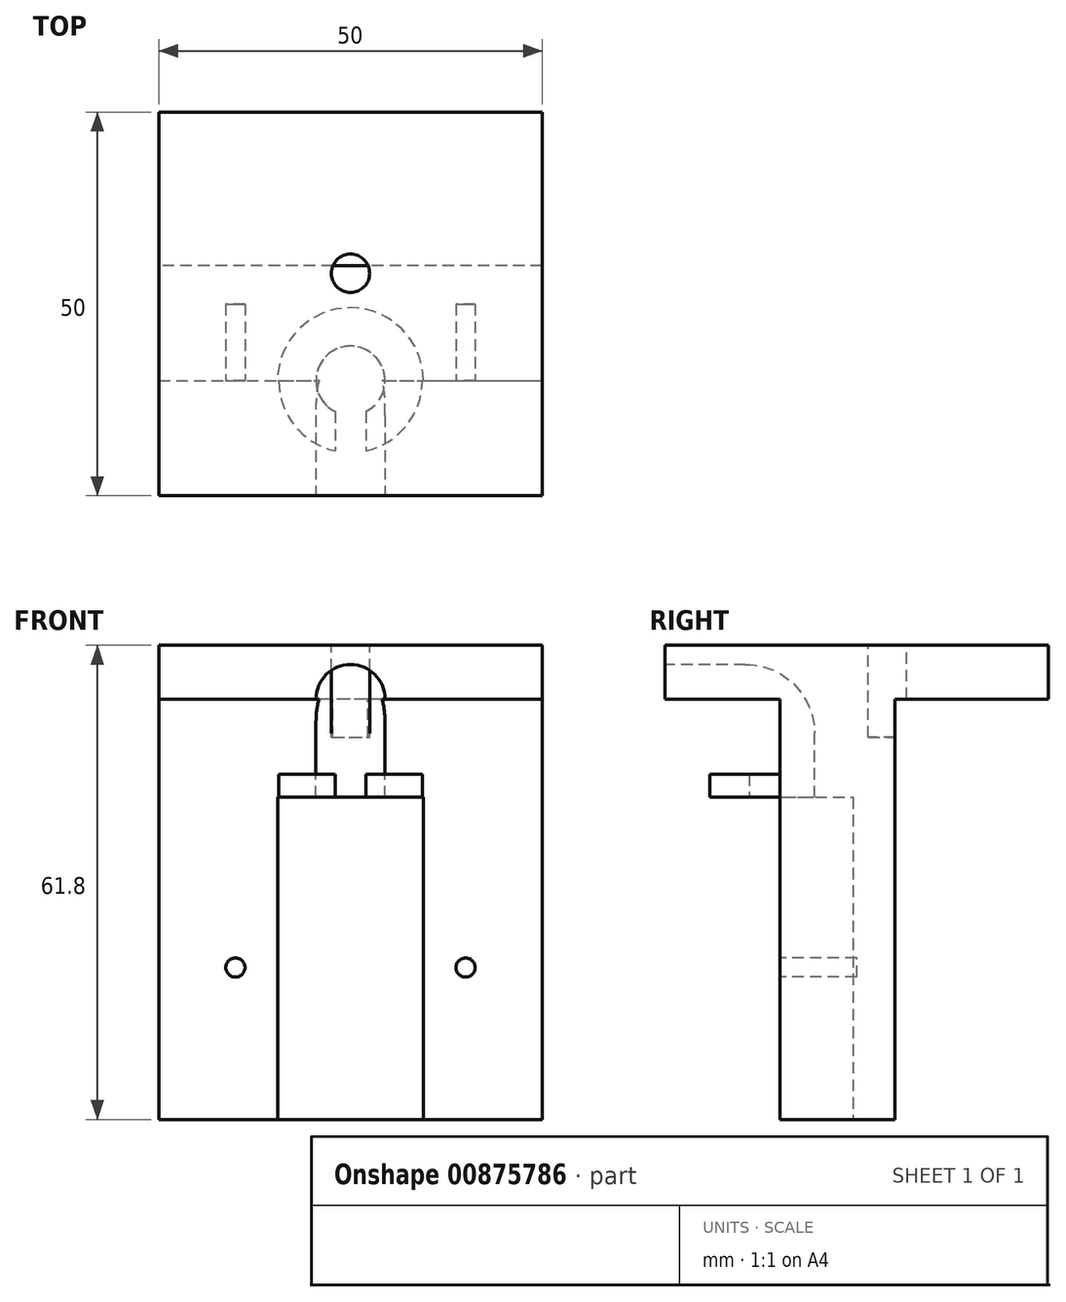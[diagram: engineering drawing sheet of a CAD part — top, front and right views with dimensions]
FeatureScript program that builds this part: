
annotation { "Feature Type Name" : "Feature", "Feature Type Description" : "" }
export const myFeature = defineFeature(function(context is Context, id is Id, definition is map)
    precondition{}
    {
        {
            var Q0;
            Q0=qCreatedBy(makeId("Top.planeOp"),FACE);
            var sketch = newSketch(context, id + "F0", { "sketchPlane" : qUnion([Q0])});
            skLineSegment(sketch, "E0", {"start": v(0, 0) * mm, "end": v(0, -25) * mm, "construction": true});
            skLineSegment(sketch, "E1", {"start": v(0, -25) * mm, "end": v(25, -25) * mm});
            skLineSegment(sketch, "E2", {"start": v(25, -25) * mm, "end": v(25, 25) * mm});
            skLineSegment(sketch, "E3", {"start": v(25, 25) * mm, "end": v(-25, 25) * mm});
            skLineSegment(sketch, "E4", {"start": v(-25, 25) * mm, "end": v(-25, -25) * mm});
            skLineSegment(sketch, "E5", {"start": v(-25, -25) * mm, "end": v(0, -25) * mm});
            skSolve(sketch);
        }
        {
            var Q0;
            Q0 = qSketchRegion(id + "F0", true);
            extrude(context, id + "F1", {"entities" : qUnion([Q0]), "depth" : 7 * mm, "offsetDistance" : 25 * mm});
        }
        {
            var Q0;
            Q0=makeQuery(id+"F1.opExtrude","CAP_FACE",FACE,{"disambiguationData":[OSD([sQuery(id+"F0.wireOp",EDGE,"E1"),sQuery(id+"F0.wireOp",EDGE,"E2"),sQuery(id+"F0.wireOp",EDGE,"E3"),sQuery(id+"F0.wireOp",EDGE,"E4"),sQuery(id+"F0.wireOp",EDGE,"E5")])],"isStart":false});
            var sketch = newSketch(context, id + "F2", { "sketchPlane" : qUnion([Q0])});
            skCircle(sketch, "E6", {"center": v(0, 4) * mm, "radius": 2.5 * mm});
            skSolve(sketch);
        }
        {
            var Q0;
            Q0=makeQuery(id+"F0.imprint","IMPRINT",FACE,{"disambiguationData":[TD([[makeQuery(id+"F0.imprint","IMPRINT",EDGE,{"derivedFrom":sQuery(id+"F0.wireOp",EDGE,"E1")}),1.0]])]});
            var sketch = newSketch(context, id + "F3", { "sketchPlane" : qUnion([Q0])});
            skLineSegment(sketch, "E7", {"start": v(0, 0) * mm, "end": v(0, -10) * mm, "construction": true});
            skLineSegment(sketch, "E8", {"start": v(0, -10) * mm, "end": v(25, -10) * mm});
            skLineSegment(sketch, "E9", {"start": v(25, -10) * mm, "end": v(25, 5) * mm});
            skLineSegment(sketch, "E10", {"start": v(25, 5) * mm, "end": v(-25, 5) * mm});
            skLineSegment(sketch, "E11", {"start": v(-25, 5) * mm, "end": v(-25, -10) * mm});
            skLineSegment(sketch, "E12", {"start": v(-25, -10) * mm, "end": v(0, -10) * mm});
            skSolve(sketch);
        }
        {
            var Q0;
            Q0 = qSketchRegion(id + "F3", true);
            extrude(context, id + "F4", {"entities" : qUnion([Q0]), "operationType" : NewBodyOperationType.ADD, "oppositeDirection" : true, "depth" : 54.8 * mm, "offsetDistance" : 25 * mm});
        }
        {
            var Q0;
            Q0=makeQuery(id+"F4.opExtrude","CAP_FACE",FACE,{"disambiguationData":[OSD([sQuery(id+"F3.wireOp",EDGE,"E8"),sQuery(id+"F3.wireOp",EDGE,"E9"),sQuery(id+"F3.wireOp",EDGE,"E10"),sQuery(id+"F3.wireOp",EDGE,"E11"),sQuery(id+"F3.wireOp",EDGE,"E12")])],"isStart":false});
            var sketch = newSketch(context, id + "F5", { "sketchPlane" : qUnion([Q0])});
            skLineSegment(sketch, "E13", {"start": v(0, 0) * mm, "end": v(0, 10) * mm, "construction": true});
            skCircle(sketch, "E14", {"center": v(0, 10) * mm, "radius": 9.5 * mm});
            skSolve(sketch);
        }
        {
            var Q0;
            Q0 = qSketchRegion(id + "F5", true);
            extrude(context, id + "F6", {"entities" : qUnion([Q0]), "operationType" : NewBodyOperationType.REMOVE, "oppositeDirection" : true, "depth" : 42 * mm, "offsetDistance" : 25 * mm});
        }
        {
            var Q0;
            Q0=qCreatedBy(makeId("Top.planeOp"),FACE);
            cPlane(context, id + "F7", {"entities" : qUnion([Q0]), "cplaneType" : CPlaneType.OFFSET, "offset" : 4.5 * mm, "oppositeDirection" : true, "width" : 150 * mm, "height" : 150 * mm});
        }
        {
            var Q0;
            Q0=qCreatedBy(id+"F7.planeOp",FACE);
            var sketch = newSketch(context, id + "F8", { "sketchPlane" : qUnion([Q0])});
            skLineSegment(sketch, "E15", {"start": v(0, 0) * mm, "end": v(0, -10) * mm, "construction": true});
            skCircle(sketch, "E16", {"center": v(0, -10) * mm, "radius": 4.5 * mm});
            skSolve(sketch);
        }
        {
            var Q0;
            Q0 = qSketchRegion(id + "F8", true);
            extrude(context, id + "F9", {"entities" : qUnion([Q0]), "operationType" : NewBodyOperationType.REMOVE, "oppositeDirection" : true, "depth" : 25 * mm, "offsetDistance" : 25 * mm});
        }
        {
            var Q0;
            Q0=makeQuery(id+"F1.opExtrude","SWEPT_FACE",FACE,{"disambiguationData":[OSD([sQuery(id+"F0.wireOp",EDGE,"E1"),sQuery(id+"F0.wireOp",EDGE,"E5")])]});
            var sketch = newSketch(context, id + "F10", { "sketchPlane" : qUnion([Q0])});
            skCircle(sketch, "E17", {"center": v(0, 0) * mm, "radius": 4.5 * mm});
            skSolve(sketch);
        }
        {
            var Q0;
            Q0 = qSketchRegion(id + "F10", true);
            extrude(context, id + "F11", {"entities" : qUnion([Q0]), "operationType" : NewBodyOperationType.REMOVE, "oppositeDirection" : true, "depth" : 10.5 * mm, "offsetDistance" : 25 * mm});
        }
        {
            var Q0;
            Q0=qCreatedBy(id+"F7.planeOp",FACE);
            var sketch = newSketch(context, id + "F12", { "sketchPlane" : qUnion([Q0])});
            skLineSegment(sketch, "E18", {"start": v(0, 0) * mm, "end": v(0, -10) * mm, "construction": true});
            skCircle(sketch, "E19", {"center": v(0, -10) * mm, "radius": 4.5 * mm});
            skSolve(sketch);
        }
        {
            var Q0;
            Q0=qCreatedBy(makeId("Right.planeOp"),FACE);
            var sketch = newSketch(context, id + "F13", { "sketchPlane" : qUnion([Q0])});
            skLineSegment(sketch, "E20", {"start": v(0, 0) * mm, "end": v(-14.5, 0) * mm, "construction": true});
            skLineSegment(sketch, "E21", {"start": v(-14.5, 0) * mm, "end": v(-10, 0) * mm, "construction": true});
            skLineSegment(sketch, "E22", {"start": v(-10, 0) * mm, "end": v(-10, -4.5) * mm, "construction": true});
            skArc(sketch, "E23", {"start": v(-10, -4.5) * mm, "mid": v(-11.32, -1.32) * mm, "end": v(-14.5, 0) * mm});
            skSolve(sketch);
        }
        {
            var Q0;
            Q0=makeQuery(id+"F12.imprint","IMPRINT",FACE,{"disambiguationData":[TD([[makeQuery(id+"F12.imprint","IMPRINT",EDGE,{"derivedFrom":sQuery(id+"F12.wireOp",EDGE,"E19")}),1.0]])]});
            var Q1;
            Q1=sQuery(id+"F13.wireOp",EDGE,"E23");
            sweep(context, id + "F14", {"operationType" : NewBodyOperationType.REMOVE, "profiles" : qUnion([Q0]), "path" : qUnion([Q1])});
        }
        {
            var Q0;
            {var subQ0=sQuery(id+"F3.wireOp",EDGE,"E12");var subQ2=sQuery(id+"F3.wireOp",EDGE,"E8");var subQ3=sQuery(id+"F0.wireOp",EDGE,"E2");Q0=makeQuery(id+"F14.boolean.opBoolean","SPLIT",FACE,{"disambiguationData":[TD([makeQuery(id+"F1.opExtrude","SWEPT_FACE",FACE,{"disambiguationData":[OSD([subQ3])]})])],"derivedFrom":makeQuery(id+"F4.opExtrude","SWEPT_FACE",FACE,{"disambiguationData":[OSD([subQ2,subQ0])]})});}
            var sketch = newSketch(context, id + "F15", { "sketchPlane" : qUnion([Q0])});
            skLineSegment(sketch, "E24", {"start": v(0, 0) * mm, "end": v(0, -35) * mm, "construction": true});
            skLineSegment(sketch, "E25", {"start": v(0, -35) * mm, "end": v(15, -35) * mm, "construction": true});
            skCircle(sketch, "E26", {"center": v(15, -35) * mm, "radius": 1.25 * mm});
            skCircle(sketch, "E27.MirrorC", {"center": v(-15, -35) * mm, "radius": 1.25 * mm});
            skSolve(sketch);
        }
        {
            var Q0;
            Q0 = qSketchRegion(id + "F15", true);
            extrude(context, id + "F16", {"entities" : qUnion([Q0]), "operationType" : NewBodyOperationType.REMOVE, "oppositeDirection" : true, "depth" : 10 * mm, "offsetDistance" : 25 * mm});
        }
        {
            var Q0;
            Q0=makeQuery(id+"F6.boolean.opBoolean","COPY",FACE,{"derivedFrom":makeQuery(id+"F6.opExtrude","CAP_FACE",FACE,{"disambiguationData":[OSD([sQuery(id+"F5.wireOp",EDGE,"E14")])],"isStart":false})});
            var sketch = newSketch(context, id + "F17", { "sketchPlane" : qUnion([Q0])});
            skArc(sketch, "E28", {"start": v(-2.02, 19.13) * mm, "mid": v(0, 0.65) * mm, "end": v(2.02, 19.13) * mm});
            skArc(sketch, "E29", {"start": v(-2.02, 14.02) * mm, "mid": v(0, 5.5) * mm, "end": v(2.02, 14.02) * mm});
            skLineSegment(sketch, "E30", {"start": v(0, 10) * mm, "end": v(2.02, 10) * mm, "construction": true});
            skLineSegment(sketch, "E31", {"start": v(2.02, 14.02) * mm, "end": v(2.02, 19.13) * mm});
            skLineSegment(sketch, "E32.MirrorCS", {"start": v(-2.02, 14.02) * mm, "end": v(-2.02, 19.13) * mm});
            skPoint(sketch, "E33", {"position": v(2.02, 19.13) * mm});
            skPoint(sketch, "E34", {"position": v(2.02, 14.02) * mm});
            skPoint(sketch, "E35", {"position": v(-2.02, 14.02) * mm});
            skPoint(sketch, "E36", {"position": v(-2.02, 19.13) * mm});
            skPoint(sketch, "E37.orphan", {"position": v(-2.02, 10) * mm});
            skPoint(sketch, "E38.orphan", {"position": v(2.02, 20.89) * mm});
            skPoint(sketch, "E39.orphan", {"position": v(-2.02, 20.89) * mm});
            skLineSegment(sketch, "E40", {"start": v(0, 0) * mm, "end": v(-25.02, 0) * mm, "construction": true});
            skLineSegment(sketch, "E41", {"start": v(-25.02, 0) * mm, "end": v(-25.02, -5) * mm, "construction": true});
            skLineSegment(sketch, "E42", {"start": v(-25.02, -5) * mm, "end": v(-25.02, 10) * mm, "construction": true});
            skSolve(sketch);
        }
        {
            var Q0;
            Q0 = qSketchRegion(id + "F17", true);
            extrude(context, id + "F18", {"entities" : qUnion([Q0]), "operationType" : NewBodyOperationType.ADD, "oppositeDirection" : true, "depth" : 3 * mm, "offsetDistance" : 25 * mm});
        }
        {
            var Q0;
            Q0 = qSketchRegion(id + "F2", true);
            extrude(context, id + "F19", {"entities" : qUnion([Q0]), "operationType" : NewBodyOperationType.REMOVE, "oppositeDirection" : true, "depth" : 12 * mm, "offsetDistance" : 25 * mm});
        }
    });
